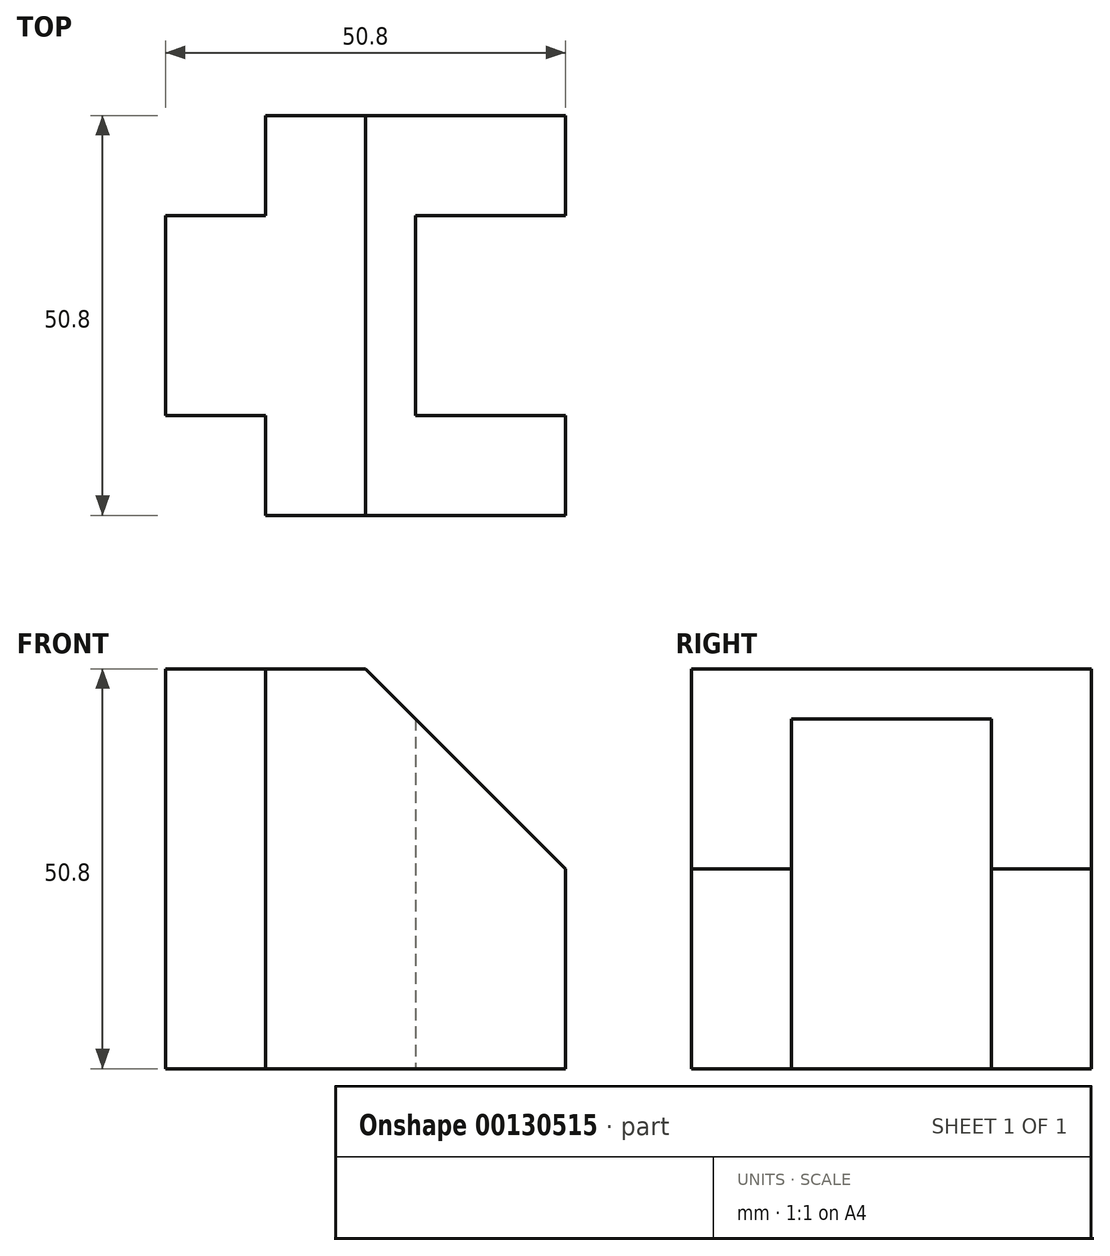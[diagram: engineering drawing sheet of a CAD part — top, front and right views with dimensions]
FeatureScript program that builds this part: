
annotation { "Feature Type Name" : "Feature", "Feature Type Description" : "" }
export const myFeature = defineFeature(function(context is Context, id is Id, definition is map)
    precondition{}
    {
        {
            var Q0;
            Q0=qCreatedBy(makeId("Front.planeOp"),FACE);
            var sketch = newSketch(context, id + "F0", { "sketchPlane" : qUnion([Q0])});
            skLineSegment(sketch, "E0.bottom", {"start": v(0, 0) * mm, "end": v(50.8, 0) * mm});
            skLineSegment(sketch, "E0.top", {"start": v(0, 50.8) * mm, "end": v(25.4, 50.8) * mm});
            skLineSegment(sketch, "E0.left", {"start": v(0, 0) * mm, "end": v(0, 50.8) * mm});
            skLineSegment(sketch, "E0.right", {"start": v(50.8, 0) * mm, "end": v(50.8, 25.4) * mm});
            skLineSegment(sketch, "E1", {"start": v(25.4, 50.8) * mm, "end": v(50.8, 25.4) * mm});
            skSolve(sketch);
        }
        {
            var Q0;
            Q0=makeQuery(id+"F0.imprint","IMPRINT",FACE,{"disambiguationData":[TD([[makeQuery(id+"F0.imprint","IMPRINT",EDGE,{"derivedFrom":sQuery(id+"F0.wireOp",EDGE,"E0.bottom")}),1.0]])]});
            extrude(context, id + "F1", {"entities" : qUnion([Q0]), "endBound" : BoundingType.SYMMETRIC, "depth" : 50.8 * mm});
        }
        {
            var Q0;
            Q0=makeQuery(id+"F1.opExtrude","SWEPT_FACE",FACE,{"disambiguationData":[OSD([sQuery(id+"F0.wireOp",EDGE,"E0.top")])]});
            var sketch = newSketch(context, id + "F2", { "sketchPlane" : qUnion([Q0])});
            skLineSegment(sketch, "E2.bottom", {"start": v(0, 25.4) * mm, "end": v(12.7, 25.4) * mm});
            skLineSegment(sketch, "E2.top", {"start": v(0, 12.7) * mm, "end": v(12.7, 12.7) * mm});
            skLineSegment(sketch, "E2.left", {"start": v(0, 25.4) * mm, "end": v(0, 12.7) * mm});
            skLineSegment(sketch, "E2.right", {"start": v(12.7, 25.4) * mm, "end": v(12.7, 12.7) * mm});
            skPoint(sketch, "E3.oppositeSnap0", {"position": v(12.7, 19.05) * mm});
            skLineSegment(sketch, "E3.bottom", {"start": v(0, -25.4) * mm, "end": v(12.7, -25.4) * mm});
            skLineSegment(sketch, "E3.top", {"start": v(0, -12.7) * mm, "end": v(12.7, -12.7) * mm});
            skLineSegment(sketch, "E3.left", {"start": v(0, -25.4) * mm, "end": v(0, -12.7) * mm});
            skLineSegment(sketch, "E3.right", {"start": v(12.7, -25.4) * mm, "end": v(12.7, -12.7) * mm});
            skSolve(sketch);
        }
        {
            var Q0;
            Q0=makeQuery(id+"F2.imprint","IMPRINT",FACE,{"disambiguationData":[TD([[makeQuery(id+"F2.imprint","IMPRINT",EDGE,{"derivedFrom":sQuery(id+"F2.wireOp",EDGE,"E2.bottom")}),-1.0]])]});
            var Q1;
            Q1=makeQuery(id+"F2.imprint","IMPRINT",FACE,{"disambiguationData":[TD([[makeQuery(id+"F2.imprint","IMPRINT",EDGE,{"derivedFrom":sQuery(id+"F2.wireOp",EDGE,"E3.bottom")}),1.0]])]});
            extrude(context, id + "F3", {"entities" : qUnion([Q0, Q1]), "operationType" : NewBodyOperationType.REMOVE, "endBound" : BoundingType.THROUGH_ALL, "oppositeDirection" : true, "depth" : 25.4 * mm});
        }
        {
            var Q0;
            Q0=makeQuery(id+"F1.opExtrude","SWEPT_FACE",FACE,{"disambiguationData":[OSD([sQuery(id+"F0.wireOp",EDGE,"E0.bottom")])]});
            var sketch = newSketch(context, id + "F4", { "sketchPlane" : qUnion([Q0])});
            skLineSegment(sketch, "E4.bottom", {"start": v(50.8, 12.7) * mm, "end": v(31.75, 12.7) * mm});
            skLineSegment(sketch, "E4.top", {"start": v(50.8, -12.7) * mm, "end": v(31.75, -12.7) * mm});
            skLineSegment(sketch, "E4.left", {"start": v(50.8, 12.7) * mm, "end": v(50.8, -12.7) * mm});
            skLineSegment(sketch, "E4.right", {"start": v(31.75, 12.7) * mm, "end": v(31.75, -12.7) * mm});
            skSolve(sketch);
        }
        {
            var Q0;
            Q0=makeQuery(id+"F4.imprint","IMPRINT",FACE,{"disambiguationData":[TD([[makeQuery(id+"F4.imprint","IMPRINT",EDGE,{"derivedFrom":sQuery(id+"F4.wireOp",EDGE,"E4.bottom")}),1.0]])]});
            extrude(context, id + "F5", {"entities" : qUnion([Q0]), "operationType" : NewBodyOperationType.REMOVE, "endBound" : BoundingType.THROUGH_ALL, "oppositeDirection" : true, "depth" : 25.4 * mm});
        }
    });
